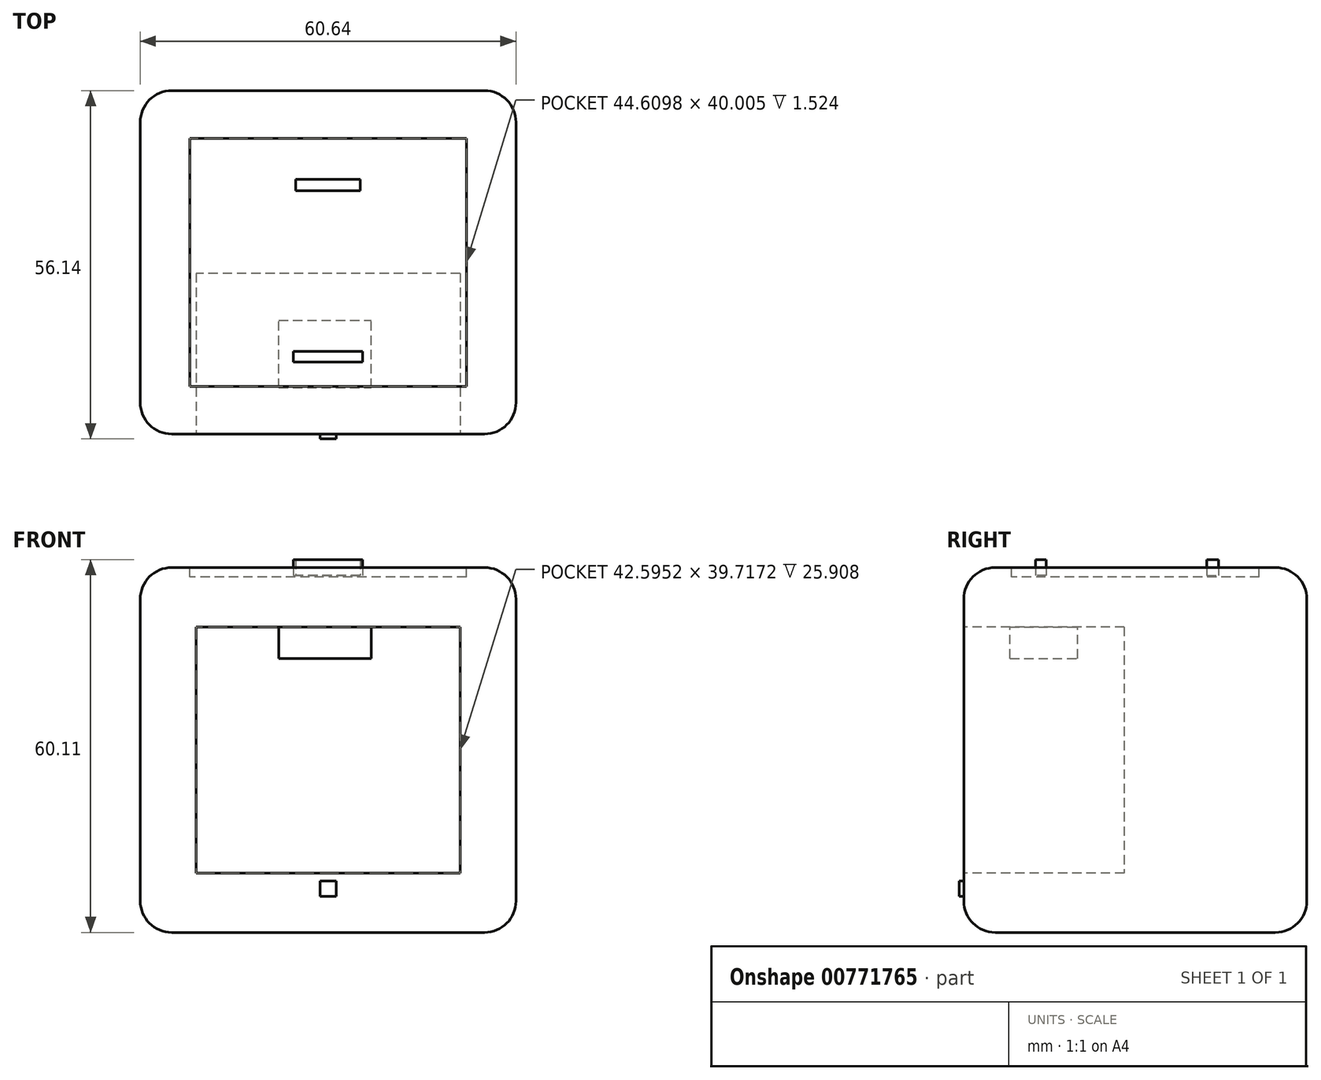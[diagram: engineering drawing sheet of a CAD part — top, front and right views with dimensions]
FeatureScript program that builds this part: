
annotation { "Feature Type Name" : "Feature", "Feature Type Description" : "" }
export const myFeature = defineFeature(function(context is Context, id is Id, definition is map)
    precondition{}
    {
        {
            var Q0;
            Q0=qCreatedBy(makeId("Front.planeOp"),FACE);
            var sketch = newSketch(context, id + "F0", { "sketchPlane" : qUnion([Q0])});
            skLineSegment(sketch, "E0.bottom", {"start": v(30.32, 29.42) * mm, "end": v(-30.32, 29.42) * mm});
            skLineSegment(sketch, "E0.top", {"start": v(30.32, -29.42) * mm, "end": v(-30.32, -29.42) * mm});
            skLineSegment(sketch, "E0.left", {"start": v(30.32, 29.42) * mm, "end": v(30.32, -29.42) * mm});
            skLineSegment(sketch, "E0.right", {"start": v(-30.32, 29.42) * mm, "end": v(-30.32, -29.42) * mm});
            skPoint(sketch, "E0.middle", {"position": v(0, 0) * mm});
            skSolve(sketch);
        }
        {
            var Q0;
            Q0=makeQuery(id+"F0.imprint","IMPRINT",FACE,{"disambiguationData":[TD([[makeQuery(id+"F0.imprint","IMPRINT",EDGE,{"derivedFrom":sQuery(id+"F0.wireOp",EDGE,"E0.bottom")}),1.0]])]});
            extrude(context, id + "F1", {"entities" : qUnion([Q0]), "endBound" : BoundingType.SYMMETRIC, "depth" : 55.37 * mm, "offsetDistance" : 25.4 * mm});
        }
        {
            var Q0;
            Q0=makeQuery(id+"F1.opExtrude","CAP_FACE",FACE,{"disambiguationData":[OSD([sQuery(id+"F0.wireOp",EDGE,"E0.bottom"),sQuery(id+"F0.wireOp",EDGE,"E0.top"),sQuery(id+"F0.wireOp",EDGE,"E0.left"),sQuery(id+"F0.wireOp",EDGE,"E0.right")])],"isStart":false});
            var sketch = newSketch(context, id + "F2", { "sketchPlane" : qUnion([Q0])});
            skLineSegment(sketch, "E1.bottom", {"start": v(21.3, 19.86) * mm, "end": v(-21.3, 19.86) * mm});
            skLineSegment(sketch, "E1.top", {"start": v(21.3, -19.86) * mm, "end": v(-21.3, -19.86) * mm});
            skLineSegment(sketch, "E1.left", {"start": v(21.3, 19.86) * mm, "end": v(21.3, -19.86) * mm});
            skLineSegment(sketch, "E1.right", {"start": v(-21.3, 19.86) * mm, "end": v(-21.3, -19.86) * mm});
            skPoint(sketch, "E1.middle", {"position": v(0, 0) * mm});
            skSolve(sketch);
        }
        {
            var Q0;
            Q0=makeQuery(id+"F2.imprint","IMPRINT",FACE,{"disambiguationData":[TD([[makeQuery(id+"F2.imprint","IMPRINT",EDGE,{"derivedFrom":sQuery(id+"F2.wireOp",EDGE,"E1.bottom")}),1.0]])]});
            extrude(context, id + "F3", {"entities" : qUnion([Q0]), "operationType" : NewBodyOperationType.REMOVE, "endBound" : BoundingType.SYMMETRIC, "oppositeDirection" : true, "depth" : 51.82 * mm, "offsetDistance" : 25.4 * mm});
        }
        {
            var Q0;
            Q0=makeQuery(id+"F1.opExtrude","CAP_EDGE",EDGE,{"disambiguationData":[OSD([sQuery(id+"F0.wireOp",EDGE,"E0.bottom")])],"isStart":false});
            fillet(context, id + "F4", {"entities" : qUnion([Q0]), "radius" : 5.08 * mm, "tangentPropagation" : true, "allowEdgeOverflow" : false});
        }
        {
            var Q0;
            Q0=makeQuery(id+"F1.opExtrude","SWEPT_EDGE",EDGE,{"disambiguationData":[OSD([sQuery(id+"F0.wireOp",EDGE,"E0.bottom"),sQuery(id+"F0.wireOp",EDGE,"E0.left")])]});
            fillet(context, id + "F5", {"entities" : qUnion([Q0]), "radius" : 5.08 * mm, "tangentPropagation" : true, "allowEdgeOverflow" : false});
        }
        {
            var Q0;
            Q0=makeQuery(id+"F1.opExtrude","CAP_EDGE",EDGE,{"disambiguationData":[OSD([sQuery(id+"F0.wireOp",EDGE,"E0.top")])],"isStart":false});
            fillet(context, id + "F6", {"entities" : qUnion([Q0]), "radius" : 5.08 * mm, "tangentPropagation" : true, "allowEdgeOverflow" : false});
        }
        {
            var Q0;
            Q0=makeQuery(id+"F1.opExtrude","CAP_EDGE",EDGE,{"disambiguationData":[OSD([sQuery(id+"F0.wireOp",EDGE,"E0.right")])],"isStart":true});
            fillet(context, id + "F7", {"entities" : qUnion([Q0]), "radius" : 5.08 * mm, "tangentPropagation" : true, "allowEdgeOverflow" : false});
        }
        {
            var Q0;
            Q0=makeQuery(id+"F1.opExtrude","SWEPT_EDGE",EDGE,{"disambiguationData":[OSD([sQuery(id+"F0.wireOp",EDGE,"E0.top"),sQuery(id+"F0.wireOp",EDGE,"E0.right")])]});
            fillet(context, id + "F8", {"entities" : qUnion([Q0]), "radius" : 5.08 * mm, "tangentPropagation" : true, "allowEdgeOverflow" : false});
        }
        {
            var Q0;
            Q0=makeQuery(id+"F3.boolean.opBoolean","COPY",FACE,{"derivedFrom":makeQuery(id+"F3.opExtrude","SWEPT_FACE",FACE,{"disambiguationData":[OSD([sQuery(id+"F2.wireOp",EDGE,"E1.bottom")])]})});
            var sketch = newSketch(context, id + "F9", { "sketchPlane" : qUnion([Q0])});
            skLineSegment(sketch, "E2.bottom", {"start": v(-7.95, 20.22) * mm, "end": v(6.95, 20.22) * mm});
            skLineSegment(sketch, "E2.top", {"start": v(-7.95, 9.33) * mm, "end": v(6.95, 9.33) * mm});
            skLineSegment(sketch, "E2.left", {"start": v(-7.95, 20.22) * mm, "end": v(-7.95, 9.33) * mm});
            skLineSegment(sketch, "E2.right", {"start": v(6.95, 20.22) * mm, "end": v(6.95, 9.33) * mm});
            skSolve(sketch);
        }
        {
            var Q0;
            Q0=makeQuery(id+"F9.imprint","IMPRINT",FACE,{"disambiguationData":[TD([[makeQuery(id+"F9.imprint","IMPRINT",EDGE,{"derivedFrom":sQuery(id+"F9.wireOp",EDGE,"E2.bottom")}),-1.0]])]});
            extrude(context, id + "F10", {"entities" : qUnion([Q0]), "operationType" : NewBodyOperationType.ADD, "depth" : 5.08 * mm, "offsetDistance" : 25.4 * mm});
        }
        {
            var Q0;
            Q0=makeQuery(id+"F1.opExtrude","SWEPT_FACE",FACE,{"disambiguationData":[OSD([sQuery(id+"F0.wireOp",EDGE,"E0.bottom")])]});
            var sketch = newSketch(context, id + "F11", { "sketchPlane" : qUnion([Q0])});
            skLineSegment(sketch, "E3.bottom", {"start": v(22.3, 20) * mm, "end": v(-22.3, 20) * mm});
            skLineSegment(sketch, "E3.top", {"start": v(22.3, -20) * mm, "end": v(-22.3, -20) * mm});
            skLineSegment(sketch, "E3.left", {"start": v(22.3, 20) * mm, "end": v(22.3, -20) * mm});
            skLineSegment(sketch, "E3.right", {"start": v(-22.3, 20) * mm, "end": v(-22.3, -20) * mm});
            skPoint(sketch, "E3.middle", {"position": v(0, 0) * mm});
            skSolve(sketch);
        }
        {
            var Q0;
            Q0=makeQuery(id+"F11.imprint","IMPRINT",FACE,{"disambiguationData":[TD([[makeQuery(id+"F11.imprint","IMPRINT",EDGE,{"derivedFrom":sQuery(id+"F11.wireOp",EDGE,"E3.bottom")}),1.0]])]});
            var sketch = newSketch(context, id + "F12", { "sketchPlane" : qUnion([Q0])});
            skLineSegment(sketch, "E4", {"start": v(-21.15, 0) * mm, "end": v(22.3, 0) * mm});
            skSolve(sketch);
        }
        {
            var Q0;
            Q0=makeQuery(id+"F11.imprint","IMPRINT",FACE,{"disambiguationData":[TD([[makeQuery(id+"F11.imprint","IMPRINT",EDGE,{"derivedFrom":sQuery(id+"F11.wireOp",EDGE,"E3.bottom")}),1.0]])]});
            extrude(context, id + "F13", {"entities" : qUnion([Q0]), "operationType" : NewBodyOperationType.REMOVE, "endBound" : BoundingType.SYMMETRIC, "oppositeDirection" : true, "depth" : 3.05 * mm, "offsetDistance" : 25.4 * mm});
        }
        {
            var Q0;
            {var subQ1=makeQuery(id+"F11.imprint","IMPRINT",EDGE,{"derivedFrom":sQuery(id+"F11.wireOp",EDGE,"E3.bottom")});Q0=makeQuery(id+"F12.imprint","IMPRINT",FACE,{"disambiguationData":[TD([[makeQuery(id+"F12.imprint","IMPRINT",EDGE,{"derivedFrom":subQ1}),1.0]])]});}
            var sketch = newSketch(context, id + "F14", { "sketchPlane" : qUnion([Q0])});
            skLineSegment(sketch, "E5.bottom", {"start": v(-6.16, 13.1) * mm, "end": v(6.16, 13.1) * mm});
            skLineSegment(sketch, "E5.top", {"start": v(-6.16, 14.82) * mm, "end": v(6.16, 14.82) * mm});
            skLineSegment(sketch, "E5.left", {"start": v(-6.16, 13.1) * mm, "end": v(-6.16, 14.82) * mm});
            skLineSegment(sketch, "E5.right", {"start": v(6.16, 13.1) * mm, "end": v(6.16, 14.82) * mm});
            skPoint(sketch, "E5.middle", {"position": v(0, 13.96) * mm});
            skLineSegment(sketch, "E6.bottom", {"start": v(-5.59, -14.37) * mm, "end": v(5.59, -14.37) * mm});
            skLineSegment(sketch, "E6.top", {"start": v(-5.59, -16.09) * mm, "end": v(5.59, -16.09) * mm});
            skLineSegment(sketch, "E6.left", {"start": v(-5.59, -14.37) * mm, "end": v(-5.59, -16.09) * mm});
            skLineSegment(sketch, "E6.right", {"start": v(5.59, -14.37) * mm, "end": v(5.59, -16.09) * mm});
            skPoint(sketch, "E6.middle", {"position": v(0, -15.23) * mm});
            skSolve(sketch);
        }
        {
            var Q0;
            Q0=makeQuery(id+"F14.imprint","IMPRINT",FACE,{"disambiguationData":[TD([[makeQuery(id+"F14.imprint","IMPRINT",EDGE,{"derivedFrom":sQuery(id+"F14.wireOp",EDGE,"E6.bottom")}),-1.0]])]});
            extrude(context, id + "F15", {"entities" : qUnion([Q0]), "endBound" : BoundingType.SYMMETRIC, "depth" : 2.54 * mm, "offsetDistance" : 25.4 * mm});
        }
        {
            var Q0;
            {var subQ1=makeQuery(id+"F11.imprint","IMPRINT",EDGE,{"derivedFrom":sQuery(id+"F11.wireOp",EDGE,"E3.bottom")});Q0=makeQuery(id+"F12.imprint","IMPRINT",FACE,{"disambiguationData":[TD([[makeQuery(id+"F12.imprint","IMPRINT",EDGE,{"derivedFrom":subQ1}),1.0]])]});}
            var sketch = newSketch(context, id + "F16", { "sketchPlane" : qUnion([Q0])});
            skLineSegment(sketch, "E7.bottom", {"start": v(5.21, 11.52) * mm, "end": v(-5.21, 11.52) * mm});
            skLineSegment(sketch, "E7.top", {"start": v(5.21, 13.41) * mm, "end": v(-5.21, 13.41) * mm});
            skLineSegment(sketch, "E7.left", {"start": v(5.21, 11.52) * mm, "end": v(5.21, 13.41) * mm});
            skLineSegment(sketch, "E7.right", {"start": v(-5.21, 11.52) * mm, "end": v(-5.21, 13.41) * mm});
            skPoint(sketch, "E7.middle", {"position": v(0, 12.47) * mm});
            skSolve(sketch);
        }
        {
            var Q0;
            Q0=makeQuery(id+"F16.imprint","IMPRINT",FACE,{"disambiguationData":[TD([[makeQuery(id+"F16.imprint","IMPRINT",EDGE,{"derivedFrom":sQuery(id+"F16.wireOp",EDGE,"E7.bottom")}),-1.0]])]});
            extrude(context, id + "F17", {"entities" : qUnion([Q0]), "endBound" : BoundingType.SYMMETRIC, "depth" : 2.54 * mm, "offsetDistance" : 25.4 * mm});
        }
        {
            var Q0;
            Q0=makeQuery(id+"F1.opExtrude","CAP_FACE",FACE,{"disambiguationData":[OSD([sQuery(id+"F0.wireOp",EDGE,"E0.bottom"),sQuery(id+"F0.wireOp",EDGE,"E0.top"),sQuery(id+"F0.wireOp",EDGE,"E0.left"),sQuery(id+"F0.wireOp",EDGE,"E0.right")])],"isStart":false});
            var sketch = newSketch(context, id + "F18", { "sketchPlane" : qUnion([Q0])});
            skLineSegment(sketch, "E8.bottom", {"start": v(1.32, -23.6) * mm, "end": v(-1.32, -23.6) * mm});
            skLineSegment(sketch, "E8.top", {"start": v(1.32, -21.14) * mm, "end": v(-1.32, -21.14) * mm});
            skLineSegment(sketch, "E8.left", {"start": v(1.32, -23.6) * mm, "end": v(1.32, -21.14) * mm});
            skLineSegment(sketch, "E8.right", {"start": v(-1.32, -23.6) * mm, "end": v(-1.32, -21.14) * mm});
            skPoint(sketch, "E8.middle", {"position": v(0, -22.37) * mm});
            skSolve(sketch);
        }
        {
            var Q0;
            Q0=makeQuery(id+"F18.imprint","IMPRINT",FACE,{"disambiguationData":[TD([[makeQuery(id+"F18.imprint","IMPRINT",EDGE,{"derivedFrom":sQuery(id+"F18.wireOp",EDGE,"E8.bottom")}),-1.0]])]});
            extrude(context, id + "F19", {"entities" : qUnion([Q0]), "depth" : 0.76 * mm, "offsetDistance" : 25.4 * mm});
        }
    });
